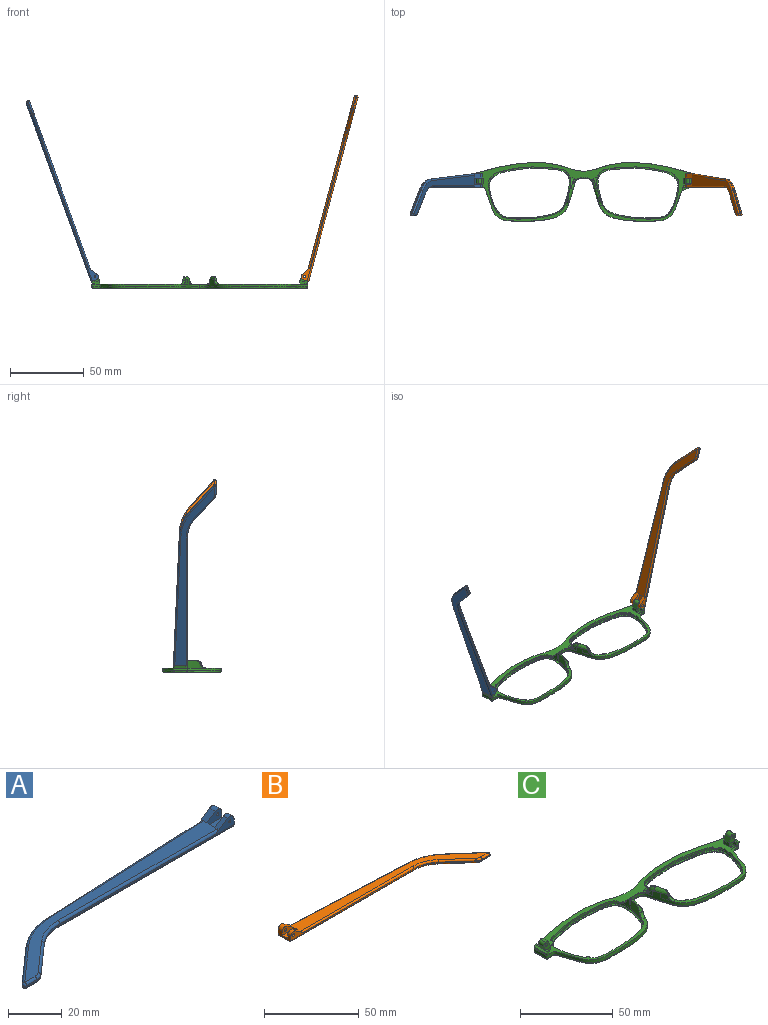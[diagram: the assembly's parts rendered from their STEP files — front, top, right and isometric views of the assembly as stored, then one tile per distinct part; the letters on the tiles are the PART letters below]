
ASSEMBLY  parts=3 mates=2
PART A: 43 faces, bbox 130.2x29.5x5.9 mm
  f0: plane 9.62x3.72mm, normal (1,0,0), area 24.7mm2, adj f1,f3,f4,f5,f10,f16,f18,f28
  f1: cylinder r=2.2mm len=3.45mm, axis (0,-1,0), area 11mm2, adj f0,f2,f4,f37
  f2: plane 6.01x3.91mm, normal (-0.55,0,0.84), area 12.7mm2, adj f1,f4,f9,f19,f37
  f3: plane 2.26x0.1mm, normal (0,0,1), area 0.1mm2, adj f0,f5,f18
  f4: plane 92.1x4.9mm, normal (0,-1,0), area 79.9mm2, adj f0,f1,f2,f14,f19,f36,f42
  f5: plane 93.42x4.13mm, normal (-0.04,1,0), area 64.8mm2, adj f0,f3,f11,f15,f17,f27,f28
  f6: plane 17.82x15.72mm, normal (-0.66,0.75,0), area 14.3mm2, adj f11,f12,f25,f30
  f7: plane 5.46x0.6mm, normal (0,-1,0), area 3.3mm2, adj f12,f13,f23,f32
  f8: plane 14.99x13.23mm, normal (0.66,-0.75,0), area 12mm2, adj f13,f14,f21,f34
  f9: plane 121.18x26.73mm, normal (0,0,1), area 627.7mm2, adj f2,f17,f19,f20,f21,f22,f23,f25
  f10: plane 129.1x27.08mm, normal (0,0,-1), area 686.5mm2, adj f0,f28,f29,f30,f32,f33,f34,f35
  f11: cylinder r=30mm len=18.52mm, axis (0,0,-1), area 12.2mm2, adj f5,f6,f26,f29
  f12: cylinder r=1mm len=1.75mm, axis (0,0,-1), area 1.5mm2, adj f6,f7,f24,f31
  f13: cylinder r=5mm len=3.31mm, axis (0,0,-1), area 2.2mm2, adj f7,f8,f22,f33
  f14: cylinder r=20mm len=13.23mm, axis (0,0,1), area 8.7mm2, adj f4,f8,f20,f35
  f15: plane 5.66x0.25mm, normal (0,0,-1), area 0.7mm2, adj f5,f17,f18
  f16: cylinder r=2.2mm len=3.45mm, axis (0,-1,0), area 14.8mm2, adj f0,f17,f18,f38
  f17: plane 6.01x3.91mm, normal (-0.55,0,0.84), area 16.9mm2, adj f5,f9,f15,f16,f18,f27,f38
  f18: plane 7.92x3.3mm, normal (0,1,0), area 15.9mm2, adj f0,f3,f15,f16,f17,f41
  f19: cylinder r=1mm len=84.18mm, axis (-1,0,0), area 131.4mm2, adj f2,f4,f9,f20
  f20: torus R=21mm, axis (0,0,1), area 23.1mm2, adj f9,f14,f19,f21
  f21: cylinder r=1mm len=15.65mm, axis (-0.75,-0.66,0), area 31.4mm2, adj f8,f9,f20,f22
  f22: torus R=4mm, axis (0,0,1), area 5.3mm2, adj f9,f13,f21,f23
  f23: cylinder r=1mm len=5.46mm, axis (-1,0,0), area 8.6mm2, adj f7,f9,f22,f24
  f24: sphere r=1mm, area 2.4mm2, adj f12,f23,f25
  f25: cylinder r=1mm len=18.48mm, axis (0.75,0.66,0), area 37.3mm2, adj f6,f9,f24,f26
  f26: torus R=29mm, axis (0,0,1), area 31.6mm2, adj f9,f11,f25,f27
  f27: cylinder r=1mm len=85.5mm, axis (1,0.04,0), area 133.5mm2, adj f5,f9,f17,f26
  f28: cylinder r=1mm len=93.46mm, axis (-1,-0.04,0), area 146.9mm2, adj f0,f5,f10,f29
  f29: torus R=29mm, axis (0,0,1), area 31.6mm2, adj f10,f11,f28,f30
  f30: cylinder r=1mm len=18.48mm, axis (-0.75,-0.66,0), area 37.3mm2, adj f6,f10,f29,f31
  f31: sphere r=1mm, area 2.4mm2, adj f12,f30,f32
  f32: cylinder r=1mm len=5.46mm, axis (1,0,0), area 8.6mm2, adj f7,f10,f31,f33
  f33: torus R=4mm, axis (0,0,1), area 5.3mm2, adj f10,f13,f32,f34
  f34: cylinder r=1mm len=15.65mm, axis (0.75,0.66,0), area 31.4mm2, adj f8,f10,f33,f35
  f35: torus R=21mm, axis (0,0,1), area 23.1mm2, adj f10,f14,f34,f36
  f36: cylinder r=1mm len=92.1mm, axis (1,0,0), area 144.7mm2, adj f0,f4,f10,f35
  f37: plane 7.92x4.7mm, normal (0,1,0), area 27mm2, adj f0,f1,f2,f39,f40,f42
  f38: plane 7.92x4.7mm, normal (0,-1,0), area 27mm2, adj f0,f16,f17,f39,f40,f41
  f39: plane 7.92x4.1mm, normal (0,0,1), area 32.5mm2, adj f0,f37,f38,f40
  f40: plane 4.1x1.4mm, normal (1,0,0), area 5.7mm2, adj f9,f37,f38,f39
  f41: cylinder r=0.5mm len=3.1mm, axis (0,-1,0), area 9.7mm2, adj f18,f38
  f42: cylinder r=0.5mm len=2.3mm, axis (0,-1,0), area 7.2mm2, adj f4,f37
PART B: 43 faces, bbox 130.2x29.5x5.9 mm
  f0: plane 9.62x3.72mm, normal (-1,0,0), area 24.7mm2, adj f1,f3,f4,f5,f10,f16,f18,f28
  f1: cylinder r=2.2mm len=3.45mm, axis (0,-1,0), area 11mm2, adj f0,f2,f4,f37
  f2: plane 6.01x3.91mm, normal (0.55,0,0.84), area 12.7mm2, adj f1,f4,f9,f19,f37
  f3: plane 2.26x0.1mm, normal (0,0,1), area 0.1mm2, adj f0,f5,f18
  f4: plane 92.1x4.9mm, normal (0,-1,0), area 78.2mm2, adj f0,f1,f2,f14,f19,f36,f42
  f5: plane 93.42x4.13mm, normal (0.04,1,0), area 64.8mm2, adj f0,f3,f11,f15,f17,f27,f28
  f6: plane 17.82x15.72mm, normal (0.66,0.75,0), area 14.3mm2, adj f11,f12,f25,f30
  f7: plane 5.46x0.6mm, normal (0,-1,0), area 3.3mm2, adj f12,f13,f23,f32
  f8: plane 14.99x13.23mm, normal (-0.66,-0.75,0), area 12mm2, adj f13,f14,f21,f34
  f9: plane 121.18x26.73mm, normal (0,0,1), area 627.7mm2, adj f2,f17,f19,f20,f21,f22,f23,f25
  f10: plane 129.1x27.08mm, normal (0,0,-1), area 686.5mm2, adj f0,f28,f29,f30,f32,f33,f34,f35
  f11: cylinder r=30mm len=18.52mm, axis (0,0,-1), area 12.2mm2, adj f5,f6,f26,f29
  f12: cylinder r=1mm len=1.75mm, axis (0,0,-1), area 1.5mm2, adj f6,f7,f24,f31
  f13: cylinder r=5mm len=3.31mm, axis (0,0,-1), area 2.2mm2, adj f7,f8,f22,f33
  f14: cylinder r=20mm len=13.23mm, axis (0,0,1), area 8.7mm2, adj f4,f8,f20,f35
  f15: plane 5.66x0.25mm, normal (0,0,-1), area 0.7mm2, adj f5,f17,f18
  f16: cylinder r=2.2mm len=3.45mm, axis (0,-1,0), area 14.8mm2, adj f0,f17,f18,f38
  f17: plane 6.01x3.91mm, normal (0.55,0,0.84), area 16.9mm2, adj f5,f9,f15,f16,f18,f27,f38
  f18: plane 7.92x3.3mm, normal (0,1,0), area 14.3mm2, adj f0,f3,f15,f16,f17,f41
  f19: cylinder r=1mm len=84.18mm, axis (1,0,0), area 131.4mm2, adj f2,f4,f9,f20
  f20: torus R=21mm, axis (0,0,1), area 23.1mm2, adj f9,f14,f19,f21
  f21: cylinder r=1mm len=15.65mm, axis (0.75,-0.66,0), area 31.4mm2, adj f8,f9,f20,f22
  f22: torus R=4mm, axis (0,0,1), area 5.3mm2, adj f9,f13,f21,f23
  f23: cylinder r=1mm len=5.46mm, axis (1,0,0), area 8.6mm2, adj f7,f9,f22,f24
  f24: sphere r=1mm, area 2.4mm2, adj f12,f23,f25
  f25: cylinder r=1mm len=18.48mm, axis (-0.75,0.66,0), area 37.3mm2, adj f6,f9,f24,f26
  f26: torus R=29mm, axis (0,0,1), area 31.6mm2, adj f9,f11,f25,f27
  f27: cylinder r=1mm len=85.5mm, axis (-1,0.04,0), area 133.5mm2, adj f5,f9,f17,f26
  f28: cylinder r=1mm len=93.46mm, axis (1,-0.04,0), area 146.9mm2, adj f0,f5,f10,f29
  f29: torus R=29mm, axis (0,0,1), area 31.6mm2, adj f10,f11,f28,f30
  f30: cylinder r=1mm len=18.48mm, axis (0.75,-0.66,0), area 37.3mm2, adj f6,f10,f29,f31
  f31: sphere r=1mm, area 2.4mm2, adj f12,f30,f32
  f32: cylinder r=1mm len=5.46mm, axis (-1,0,0), area 8.6mm2, adj f7,f10,f31,f33
  f33: torus R=4mm, axis (0,0,1), area 5.3mm2, adj f10,f13,f32,f34
  f34: cylinder r=1mm len=15.65mm, axis (-0.75,0.66,0), area 31.4mm2, adj f8,f10,f33,f35
  f35: torus R=21mm, axis (0,0,1), area 23.1mm2, adj f10,f14,f34,f36
  f36: cylinder r=1mm len=92.1mm, axis (-1,0,0), area 144.7mm2, adj f0,f4,f10,f35
  f37: plane 7.92x4.7mm, normal (0,1,0), area 25.4mm2, adj f0,f1,f2,f39,f40,f42
  f38: plane 7.92x4.7mm, normal (0,-1,0), area 25.4mm2, adj f0,f16,f17,f39,f40,f41
  f39: plane 7.92x4.1mm, normal (0,0,1), area 32.5mm2, adj f0,f37,f38,f40
  f40: plane 4.1x1.4mm, normal (-1,0,0), area 5.7mm2, adj f9,f37,f38,f39
  f41: cylinder r=0.88mm len=3.1mm, axis (0,-1,0), area 17mm2, adj f18,f38
  f42: cylinder r=0.88mm len=2.3mm, axis (0,-1,0), area 12.6mm2, adj f4,f37
PART C: 118 faces, bbox 148.1x40.9x17.9 mm
  f0: bspline ~1.82x1.22mm, area 0.7mm2, adj f2,f7,f37,f52
  f1: plane 147.69x40.46mm, normal (0,0,1), area 858.2mm2, adj f4,f5,f6,f7,f8,f12,f20,f23
  f2: bspline ~6.1x4.93mm, area 12.7mm2, adj f0,f7,f37,f41,f43,f52,f53
  f3: plane 4.46x1.45mm, normal (0,0,1), area 0.1mm2, adj f7,f38
  f4: plane 1.23x0.04mm, normal (0,0,1), area 0mm2, adj f1,f7,f22
  f5: plane 6.97x5.07mm, normal (0,1,0), area 22.7mm2, adj f1,f20,f21,f25,f27,f28,f30,f31
  f6: plane 3.2x2.36mm, normal (0,-1,0), area 5.7mm2, adj f1,f20,f26,f29
  f7: extruded ~73.26x39.84mm, area 292.7mm2, adj f0,f1,f2,f3,f4,f8,f13,f14
  f8: extruded ~35.39x5.69mm, area 72.2mm2, adj f1,f7,f18,f67
  f9: plane 144.78x37.85mm, normal (0,0,-1), area 582.4mm2, adj f13,f15,f17,f18,f19,f71,f73,f75
  f10: plane 56.06x35.45mm, normal (0,0,1), area 127mm2, adj f11,f19
  f11: extruded ~55.69x35.36mm, area 160.5mm2, adj f10,f12
  f12: extruded ~55.69x35.36mm, area 226.3mm2, adj f1,f11,f39,f40,f41,f42,f43,f44
  f13: bspline ~73.27x30.39mm, area 161.7mm2, adj f7,f9,f14,f71
  f14: bspline ~1x1mm, area 0.8mm2, adj f7,f13,f15
  f15: bspline ~8.99x1.23mm, area 12.6mm2, adj f7,f9,f14,f16
  f16: bspline ~1.04x1mm, area 0.7mm2, adj f7,f15,f17
  f17: bspline ~45.86x8.59mm, area 59.8mm2, adj f7,f9,f16,f18
  f18: bspline ~37.01x6.7mm, area 56.6mm2, adj f8,f9,f17,f76
  f19: bspline ~56.23x35.9mm, area 235.3mm2, adj f9,f10
  f20: plane 4x2.36mm, normal (-1,0,0), area 9.5mm2, adj f1,f5,f6,f21
  f21: plane 4x0.02mm, normal (0.34,0,0.94), area 0.1mm2, adj f5,f20,f28
  f22: plane 2.76x2.53mm, normal (0,-1,0), area 3.9mm2, adj f4,f26,f27,f35,f56
  f23: plane 7.67x1.6mm, normal (0.94,0,-0.34), area 13mm2, adj f1,f35,f36,f56
  f24: plane 2.1x1.69mm, normal (0,1,0), area 2.8mm2, adj f1,f25,f27,f36,f56
  f25: plane 3.3x2.1mm, normal (-1,0,0), area 6.9mm2, adj f1,f5,f24,f27
  f26: plane 2.35x2.1mm, normal (-1,0,0), area 4.9mm2, adj f1,f6,f22,f27,f29
  f27: plane 9.65x1.24mm, normal (0,0,1), area 8.2mm2, adj f5,f22,f24,f25,f26,f29,f30,f56
  f28: plane 4x3.31mm, normal (-0.94,0,0.34), area 14.1mm2, adj f5,f21,f29,f32
  f29: plane 5.77x5.06mm, normal (0,-1,0), area 17mm2, adj f6,f26,f27,f28,f30,f31,f32,f33
  f30: plane 4x2.21mm, normal (0.94,0,-0.34), area 9.4mm2, adj f5,f27,f29,f33
  f31: plane 4x0.01mm, normal (0.34,0,0.94), area 0mm2, adj f5,f29,f32,f33
  f32: cylinder r=1.98mm len=4mm, axis (0,1,0), area 12.4mm2, adj f5,f28,f29,f31
  f33: cylinder r=1.98mm len=4mm, axis (0,-1,0), area 12.4mm2, adj f5,f29,f30,f31
  f34: cylinder r=0.88mm len=4mm, axis (0,-1,0), area 22mm2, adj f5,f29
  f35: cone r=1mm half-angle=20deg, axis (0,0,1), area 2.3mm2, adj f1,f22,f23,f56
  f36: cylinder r=1mm len=2.28mm, axis (-0.34,0,-0.94), area 3mm2, adj f1,f23,f24,f56
  f37: extruded ~3.67x3.11mm, area 5.9mm2, adj f0,f2,f7,f59
  f38: extruded ~4.44x3.32mm, area 15.1mm2, adj f3,f7,f42,f43,f55
  f39: extruded ~4.98x1.37mm, area 6.6mm2, adj f12,f41
  f40: plane 3.63x0.97mm, normal (0,0,1), area 0.3mm2, adj f12,f41,f43
  f41: bspline ~15.5x15.35mm, area 6.4mm2, adj f2,f12,f39,f40,f54
  f42: bspline ~7.26x7.26mm, area 6.3mm2, adj f12,f38,f43,f55
  f43: bspline ~10.29x4.84mm, area 21.4mm2, adj f2,f7,f12,f38,f40,f42
  f44: plane 3.19x1.37mm, normal (0,0,-1), area 2.1mm2, adj f12,f45
  f45: cylinder r=2.28mm len=3.17mm, axis (0,0,1), area 2.1mm2, adj f1,f12,f44,f54
  f46: plane 3.14x2.79mm, normal (0,0,-1), area 3.9mm2, adj f12,f47
  f47: cylinder r=2.28mm len=3.13mm, axis (0,0,1), area 2.5mm2, adj f1,f12,f46
  f48: plane 1.79x1.31mm, normal (0,0,-1), area 0.9mm2, adj f12,f49
  f49: cylinder r=1.3mm len=1.78mm, axis (0,0,1), area 1.3mm2, adj f1,f12,f48
  f50: plane 1.95x1.68mm, normal (0,0,-1), area 1.5mm2, adj f12,f51
  f51: cylinder r=1.3mm len=1.93mm, axis (0,0,1), area 1.5mm2, adj f1,f12,f50
  f52: bspline ~2.66x2.04mm, area 1.9mm2, adj f0,f2,f7,f53,f58
  f53: bspline ~3.55x3.47mm, area 3.7mm2, adj f1,f2,f52,f54,f58
  f54: bspline ~6.16x4.45mm, area 7.9mm2, adj f1,f12,f41,f45,f53
  f55: bspline ~3.7x3.66mm, area 7.8mm2, adj f1,f7,f12,f38,f42
  f56: plane 9.71x1.44mm, normal (0.34,0,0.94), area 13.9mm2, adj f22,f23,f24,f27,f35,f36
  f57: bspline ~6.38x2.14mm, area 2.6mm2, adj f1,f7,f58,f115
  f58: bspline ~2.1x1.46mm, area 0.6mm2, adj f7,f52,f53,f57
  f59: bspline ~5.24x1.75mm, area 0mm2, adj f7,f37
  f60: bspline ~2.19x1.4mm, area 0.7mm2, adj f61,f66,f95,f110
  f61: bspline ~6.1x4.93mm, area 12.6mm2, adj f60,f66,f95,f99,f101,f110,f111
  f62: plane 4.46x1.45mm, normal (0,0,1), area 0.1mm2, adj f66,f96
  f63: plane 1.23x0.04mm, normal (0,0,1), area 0mm2, adj f1,f66,f80
  f64: plane 6.97x5.07mm, normal (0,1,0), area 22.7mm2, adj f1,f78,f79,f83,f85,f86,f88,f89
  f65: plane 3.2x2.36mm, normal (0,-1,0), area 5.7mm2, adj f1,f78,f84,f87
  f66: extruded ~73.26x39.84mm, area 292.7mm2, adj f1,f7,f60,f61,f62,f63,f67,f71
  f67: extruded ~35.39x5.69mm, area 72.2mm2, adj f1,f8,f66,f76
  f68: plane 56.06x35.45mm, normal (0,0,1), area 127mm2, adj f69,f77
  f69: extruded ~55.69x35.36mm, area 160.5mm2, adj f68,f70
  f70: extruded ~55.69x35.36mm, area 226.4mm2, adj f1,f69,f97,f98,f99,f100,f101,f102
  f71: bspline ~73.83x30.39mm, area 161.7mm2, adj f9,f13,f66,f72
  f72: bspline ~1x1mm, area 0.8mm2, adj f66,f71,f73
  f73: bspline ~8.99x1.23mm, area 12.6mm2, adj f9,f66,f72,f74
  f74: bspline ~1.04x1mm, area 0.8mm2, adj f66,f73,f75
  f75: bspline ~45.86x8.59mm, area 59.8mm2, adj f9,f66,f74,f76
  f76: bspline ~37.01x6.7mm, area 56.6mm2, adj f9,f18,f67,f75
  f77: bspline ~56.22x35.9mm, area 235.3mm2, adj f9,f68
  f78: plane 4x2.36mm, normal (1,0,0), area 9.5mm2, adj f1,f64,f65,f79
  f79: plane 4x0.02mm, normal (-0.34,0,0.94), area 0.1mm2, adj f64,f78,f86
  f80: plane 2.76x2.53mm, normal (0,-1,0), area 3.9mm2, adj f63,f84,f85,f93,f114
  f81: plane 7.67x1.6mm, normal (-0.94,0,-0.34), area 13mm2, adj f1,f93,f94,f114
  f82: plane 2.1x1.69mm, normal (0,1,0), area 2.8mm2, adj f1,f83,f85,f94,f114
  f83: plane 3.3x2.1mm, normal (1,0,0), area 6.9mm2, adj f1,f64,f82,f85
  f84: plane 2.35x2.1mm, normal (1,0,0), area 4.9mm2, adj f1,f65,f80,f85,f87
  f85: plane 9.65x1.24mm, normal (0,0,1), area 8.2mm2, adj f64,f80,f82,f83,f84,f87,f88,f114
  f86: plane 4x3.31mm, normal (0.94,0,0.34), area 14.1mm2, adj f64,f79,f87,f90
  f87: plane 5.77x5.06mm, normal (0,-1,0), area 17mm2, adj f65,f84,f85,f86,f88,f89,f90,f91
  f88: plane 4x2.21mm, normal (-0.94,0,-0.34), area 9.4mm2, adj f64,f85,f87,f91
  f89: plane 4x0.01mm, normal (-0.34,0,0.94), area 0mm2, adj f64,f87,f90,f91
  f90: cylinder r=1.98mm len=4mm, axis (0,1,0), area 12.4mm2, adj f64,f86,f87,f89
  f91: cylinder r=1.98mm len=4mm, axis (0,-1,0), area 12.4mm2, adj f64,f87,f88,f89
  f92: cylinder r=0.88mm len=4mm, axis (0,-1,0), area 22mm2, adj f64,f87
  f93: cone r=1mm half-angle=20deg, axis (0,0,1), area 2.3mm2, adj f1,f80,f81,f114
  f94: cylinder r=1mm len=2.28mm, axis (0.34,0,-0.94), area 3mm2, adj f1,f81,f82,f114
  f95: extruded ~3.67x3.11mm, area 5.9mm2, adj f60,f61,f66,f117
  f96: extruded ~4.44x3.32mm, area 15.1mm2, adj f62,f66,f100,f101,f113
  f97: extruded ~4.98x1.36mm, area 6.6mm2, adj f70,f99
  f98: plane 3.63x0.97mm, normal (0,0,1), area 0.3mm2, adj f70,f99,f101
  f99: bspline ~15.5x15.35mm, area 6.4mm2, adj f61,f70,f97,f98,f112
  f100: bspline ~7.26x7.26mm, area 6.2mm2, adj f70,f96,f101,f113
  f101: bspline ~10.29x4.84mm, area 21.5mm2, adj f61,f66,f70,f96,f98,f100
  f102: plane 3.19x1.37mm, normal (0,0,-1), area 2.1mm2, adj f70,f103
  f103: cylinder r=2.28mm len=3.17mm, axis (0,0,1), area 2.1mm2, adj f1,f70,f102,f112
  f104: plane 3.14x2.79mm, normal (0,0,-1), area 3.9mm2, adj f70,f105
  f105: cylinder r=2.28mm len=3.13mm, axis (0,0,1), area 2.5mm2, adj f1,f70,f104
  f106: plane 1.79x1.31mm, normal (0,0,-1), area 0.9mm2, adj f70,f107
  f107: cylinder r=1.3mm len=1.78mm, axis (0,0,1), area 1.3mm2, adj f1,f70,f106
  f108: plane 1.95x1.68mm, normal (0,0,-1), area 1.5mm2, adj f70,f109
  f109: cylinder r=1.3mm len=1.93mm, axis (0,0,1), area 1.5mm2, adj f1,f70,f108
  f110: bspline ~2.65x2.03mm, area 1.9mm2, adj f60,f61,f66,f111,f116
  f111: bspline ~3.55x3.47mm, area 3.7mm2, adj f1,f61,f110,f112,f116
  f112: bspline ~5.94x4.42mm, area 7.9mm2, adj f1,f70,f99,f103,f111
  f113: bspline ~3.7x3.66mm, area 7.8mm2, adj f1,f66,f70,f96,f100
  f114: plane 9.71x1.44mm, normal (-0.34,0,0.94), area 13.9mm2, adj f80,f81,f82,f85,f93,f94
  f115: bspline ~6.38x2.14mm, area 2.6mm2, adj f1,f57,f66,f116
  f116: bspline ~2.1x1.46mm, area 0.6mm2, adj f66,f110,f111,f115
  f117: bspline ~5.24x1.75mm, area 0mm2, adj f66,f95
PLACE A rot(axis=(0,1,0),70deg) t=(-84.77,-5.75,56)mm
PLACE B rot(axis=(0,-1,0),75deg) t=(68.2,-5.75,-61.61)mm
PLACE C t=(10.15,-1.13,-5.77)mm
MATE revolute A.f1 <-> C.f90  axis (0,-1,0) through (-60.89,2.72,1.22)mm
MATE revolute B.f41 <-> C.f33  axis (0,-1,0) through (81.2,2.72,1.21)mm
